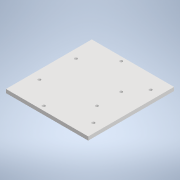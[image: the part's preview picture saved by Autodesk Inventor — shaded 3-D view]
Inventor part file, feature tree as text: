
AUTODESK INVENTOR PART (.ipt)
format: ipt  version: 2021 (Build 250183000, 183)  size: 110,592 bytes
history: native  units: mm
features: other x10, reference x9, extrude x1, sketch x1
ambient origin geometry x8: Origin, YZ Plane, XZ Plane, XY Plane, X Axis, Y Axis, Z Axis, Center Point
bodies: Body1 (feature_tree)
feature tree (21):
  other  "Sólido1"
  extrude  "Extrusión1"  Depth=260.0mm
  sketch  "Boceto1"  dims[d0=230.0mm d1=260.0mm d2=10.0mm d3=0.0mm]
  reference  "Referencia1"
  reference  "Referencia2"
  reference  "Referencia3"
  reference  "Referencia4"
  reference  "Referencia5"
  reference  "Referencia6"
  reference  "Referencia7"
  reference  "Referencia8"
  reference  "Referencia9"
  other  "<userpath>\OneDrive\Robotica\Proyecto-Rob\Piezas\Ensamble1.iam"
  other  "Ensamble1.iam"
  other  "Perno:4"
  other  "Perno:6"
  other  "Perno:2"
  other  "Perno:3"
  other  "Perno:5"
  other  "T:1"
  other  "BaseGripper:1"
